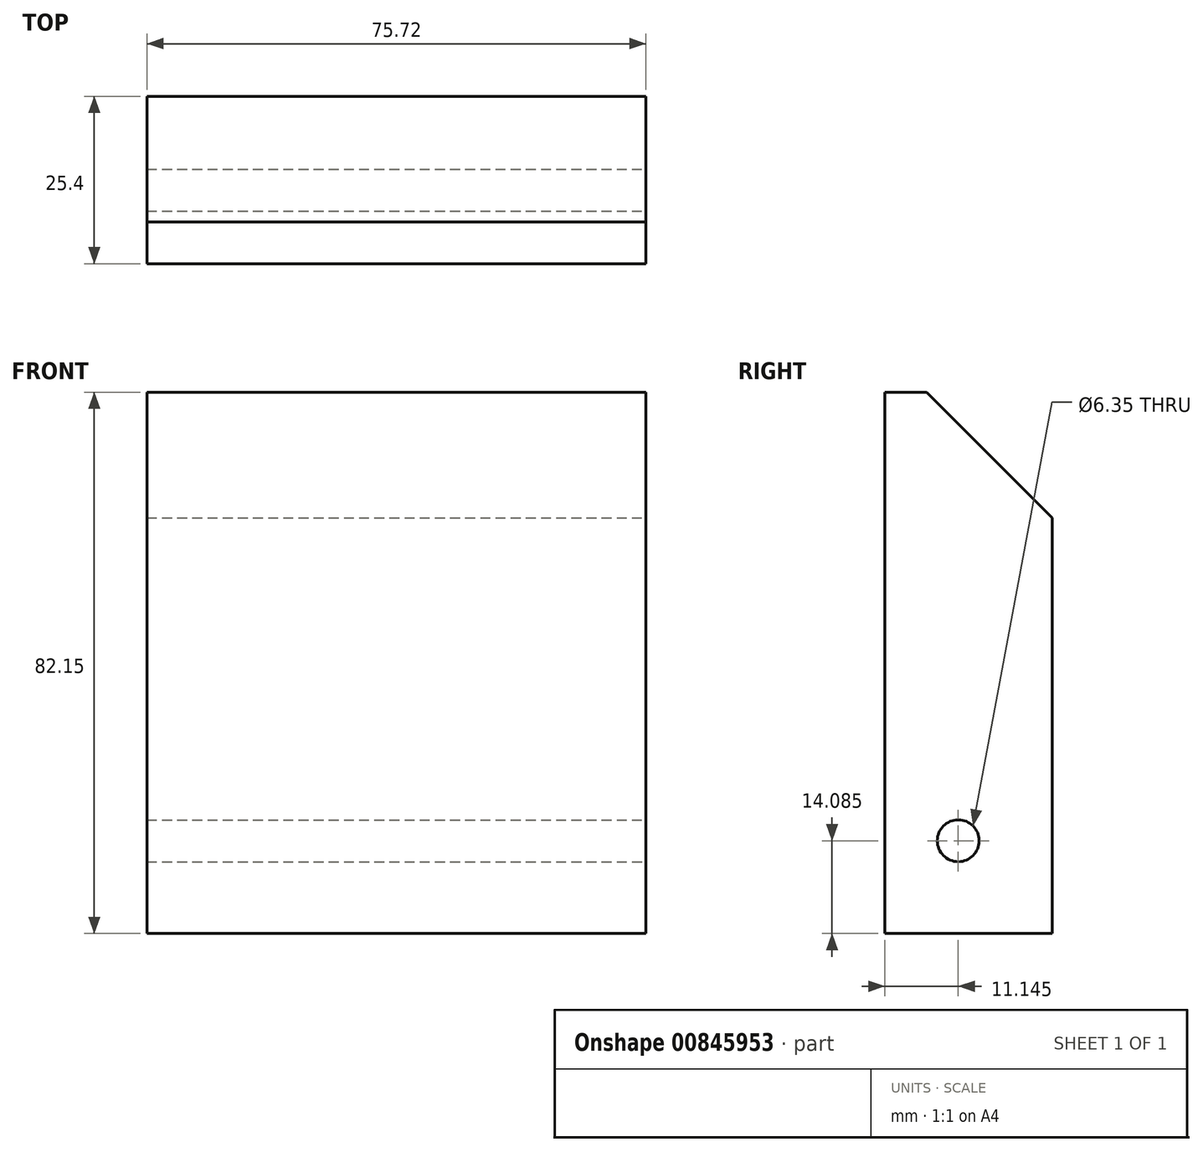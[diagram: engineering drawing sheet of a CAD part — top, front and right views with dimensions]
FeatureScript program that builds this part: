
annotation { "Feature Type Name" : "Feature", "Feature Type Description" : "" }
export const myFeature = defineFeature(function(context is Context, id is Id, definition is map)
    precondition{}
    {
        {
            var Q0;
            Q0=qCreatedBy(makeId("Front.planeOp"),FACE);
            var sketch = newSketch(context, id + "F0", { "sketchPlane" : qUnion([Q0])});
            skLineSegment(sketch, "E0.bottom", {"start": v(-37.57, -36.25) * mm, "end": v(38.15, -36.25) * mm});
            skLineSegment(sketch, "E0.top", {"start": v(-37.57, 45.9) * mm, "end": v(38.15, 45.9) * mm});
            skLineSegment(sketch, "E0.left", {"start": v(-37.57, -36.25) * mm, "end": v(-37.57, 45.9) * mm});
            skLineSegment(sketch, "E0.right", {"start": v(38.15, -36.25) * mm, "end": v(38.15, 45.9) * mm});
            skSolve(sketch);
        }
        {
            var Q0;
            Q0=makeQuery(id+"F0.imprint","IMPRINT",FACE,{"disambiguationData":[TD([[makeQuery(id+"F0.imprint","IMPRINT",EDGE,{"derivedFrom":sQuery(id+"F0.wireOp",EDGE,"E0.bottom")}),1.0]])]});
            extrude(context, id + "F1", {"entities" : qUnion([Q0]), "depth" : 25.4 * mm, "offsetDistance" : 25.4 * mm});
        }
        {
            var Q0;
            Q0=makeQuery(id+"F1.opExtrude","CAP_EDGE",EDGE,{"disambiguationData":[OSD([sQuery(id+"F0.wireOp",EDGE,"E0.top")])],"isStart":true});
            chamfer(context, id + "F2", {"entities" : qUnion([Q0]), "width" : 19.05 * mm, "tangentPropagation" : true});
        }
        {
            var Q0;
            Q0=makeQuery(id+"F1.opExtrude","SWEPT_FACE",FACE,{"disambiguationData":[OSD([sQuery(id+"F0.wireOp",EDGE,"E0.right")])]});
            var sketch = newSketch(context, id + "F3", { "sketchPlane" : qUnion([Q0])});
            skPoint(sketch, "E1", {"position": v(-14.25, -22.17) * mm});
            skSolve(sketch);
        }
        {
            var Q0;
            Q0=sQuery(id+"F3.wireOp",VERTEX,"E1");
            var Q1;
            Q1=makeQuery(id+"F1.opExtrude","SWEPT_BODY",BODY,{"disambiguationData":[OSD([sQuery(id+"F0.wireOp",EDGE,"E0.bottom"),sQuery(id+"F0.wireOp",EDGE,"E0.top"),sQuery(id+"F0.wireOp",EDGE,"E0.left"),sQuery(id+"F0.wireOp",EDGE,"E0.right")])]});
            hole(context, id + "F4", {"style" : HoleStyle.SIMPLE, "endStyle" : HoleEndStyle.THROUGH, "holeDiameter" : 6.35 * mm, "majorDiameter" : 6.35 * mm, "isTappedThrough" : true, "tappedDepth" : 12.7 * mm, "tapClearance" : 3, "locations" : qUnion([Q0]), "scope" : qUnion([Q1])});
        }
    });
